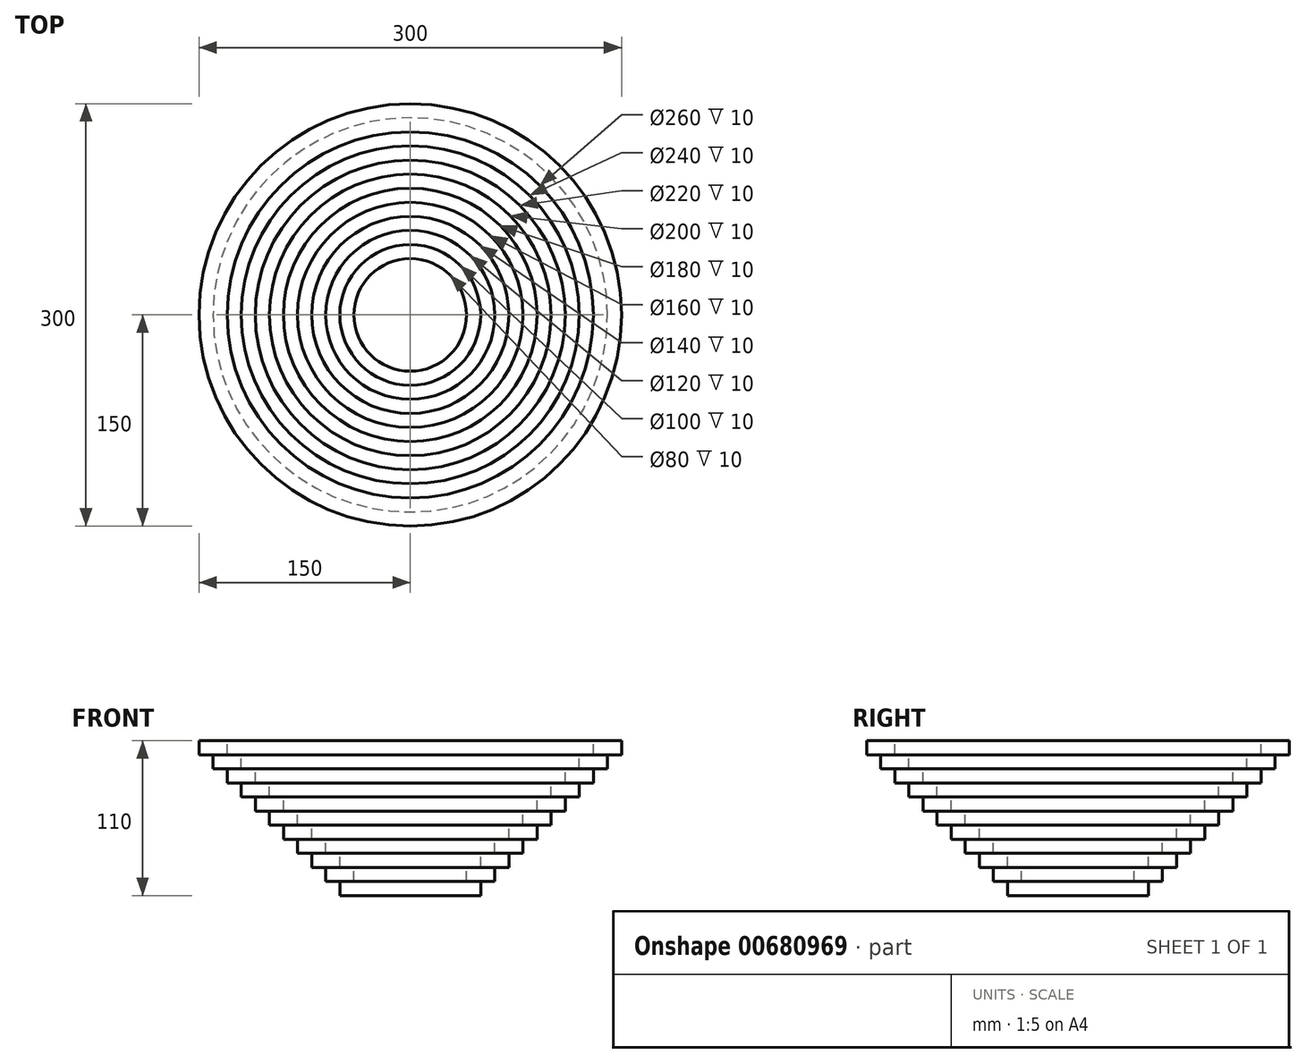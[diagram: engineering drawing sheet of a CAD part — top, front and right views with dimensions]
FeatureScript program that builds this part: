
annotation { "Feature Type Name" : "Feature", "Feature Type Description" : "" }
export const myFeature = defineFeature(function(context is Context, id is Id, definition is map)
    precondition{}
    {
        {
            var Q0;
            Q0=qCreatedBy(makeId("Front.planeOp"),FACE);
            var sketch = newSketch(context, id + "F0", { "sketchPlane" : qUnion([Q0])});
            skLineSegment(sketch, "E0", {"start": v(0, 0) * mm, "end": v(50, 0) * mm});
            skLineSegment(sketch, "E1", {"start": v(50, 0) * mm, "end": v(50, 10) * mm});
            skLineSegment(sketch, "E2", {"start": v(50, 10) * mm, "end": v(60, 10) * mm});
            skLineSegment(sketch, "E3", {"start": v(60, 10) * mm, "end": v(60, 20) * mm});
            skLineSegment(sketch, "E4", {"start": v(60, 20) * mm, "end": v(70, 20) * mm});
            skLineSegment(sketch, "E5", {"start": v(70, 20) * mm, "end": v(70, 30) * mm});
            skLineSegment(sketch, "E6", {"start": v(70, 30) * mm, "end": v(80, 30) * mm});
            skLineSegment(sketch, "E7", {"start": v(80, 30) * mm, "end": v(80, 40) * mm});
            skLineSegment(sketch, "E8", {"start": v(80, 40) * mm, "end": v(90, 40) * mm});
            skLineSegment(sketch, "E9", {"start": v(90, 40) * mm, "end": v(90, 50) * mm});
            skLineSegment(sketch, "E10", {"start": v(90, 50) * mm, "end": v(100, 50) * mm});
            skLineSegment(sketch, "E11", {"start": v(100, 50) * mm, "end": v(100, 60) * mm});
            skLineSegment(sketch, "E12", {"start": v(100, 60) * mm, "end": v(110, 60) * mm});
            skLineSegment(sketch, "E13", {"start": v(110, 60) * mm, "end": v(110, 70) * mm});
            skLineSegment(sketch, "E14", {"start": v(110, 70) * mm, "end": v(120, 70) * mm});
            skLineSegment(sketch, "E15", {"start": v(120, 70) * mm, "end": v(120, 80) * mm});
            skLineSegment(sketch, "E16", {"start": v(120, 80) * mm, "end": v(130, 80) * mm});
            skLineSegment(sketch, "E17", {"start": v(130, 80) * mm, "end": v(130, 90) * mm});
            skLineSegment(sketch, "E18", {"start": v(130, 90) * mm, "end": v(140, 90) * mm});
            skLineSegment(sketch, "E19", {"start": v(140, 90) * mm, "end": v(140, 100) * mm});
            skLineSegment(sketch, "E20", {"start": v(140, 100) * mm, "end": v(150, 100) * mm});
            skLineSegment(sketch, "E21", {"start": v(150, 100) * mm, "end": v(150, 110) * mm});
            skLineSegment(sketch, "E22.0", {"start": v(130, 100) * mm, "end": v(130, 110) * mm});
            skLineSegment(sketch, "E22.1", {"start": v(120, 100) * mm, "end": v(130, 100) * mm});
            skLineSegment(sketch, "E22.2", {"start": v(120, 90) * mm, "end": v(120, 100) * mm});
            skLineSegment(sketch, "E22.3", {"start": v(110, 90) * mm, "end": v(120, 90) * mm});
            skLineSegment(sketch, "E22.4", {"start": v(110, 80) * mm, "end": v(110, 90) * mm});
            skLineSegment(sketch, "E22.5", {"start": v(100, 80) * mm, "end": v(110, 80) * mm});
            skLineSegment(sketch, "E22.6", {"start": v(100, 70) * mm, "end": v(100, 80) * mm});
            skLineSegment(sketch, "E22.7", {"start": v(90, 70) * mm, "end": v(100, 70) * mm});
            skLineSegment(sketch, "E22.8", {"start": v(90, 60) * mm, "end": v(90, 70) * mm});
            skLineSegment(sketch, "E22.9", {"start": v(80, 60) * mm, "end": v(90, 60) * mm});
            skLineSegment(sketch, "E22.10", {"start": v(50, 20) * mm, "end": v(50, 30) * mm});
            skLineSegment(sketch, "E22.11", {"start": v(40, 20) * mm, "end": v(50, 20) * mm});
            skLineSegment(sketch, "E22.12", {"start": v(40, 10) * mm, "end": v(40, 20) * mm});
            skLineSegment(sketch, "E22.13", {"start": v(0, 10) * mm, "end": v(40, 10) * mm});
            skLineSegment(sketch, "E22.14", {"start": v(50, 30) * mm, "end": v(60, 30) * mm});
            skLineSegment(sketch, "E22.15", {"start": v(60, 30) * mm, "end": v(60, 40) * mm});
            skLineSegment(sketch, "E22.16", {"start": v(60, 40) * mm, "end": v(70, 40) * mm});
            skLineSegment(sketch, "E22.17", {"start": v(70, 40) * mm, "end": v(70, 50) * mm});
            skLineSegment(sketch, "E22.18", {"start": v(70, 50) * mm, "end": v(80, 50) * mm});
            skLineSegment(sketch, "E22.19", {"start": v(80, 50) * mm, "end": v(80, 60) * mm});
            skLineSegment(sketch, "E23", {"start": v(150, 110) * mm, "end": v(130, 110) * mm});
            skLineSegment(sketch, "E24", {"start": v(0, 10) * mm, "end": v(0, 0) * mm});
            skSolve(sketch);
        }
        {
            var Q0;
            Q0=makeQuery(id+"F0.imprint","IMPRINT",FACE,{"disambiguationData":[TD([[makeQuery(id+"F0.imprint","IMPRINT",EDGE,{"derivedFrom":sQuery(id+"F0.wireOp",EDGE,"E0")}),1.0]])]});
            var Q1;
            Q1=sQuery(id+"F0.wireOp",EDGE,"E24");
            revolve(context, id + "F1", {"surfaceOperationType" : NewSurfaceOperationType.NEW, "entities" : qUnion([Q0]), "axis" : qUnion([Q1]), "revolveType" : RevolveType.FULL});
        }
    });
